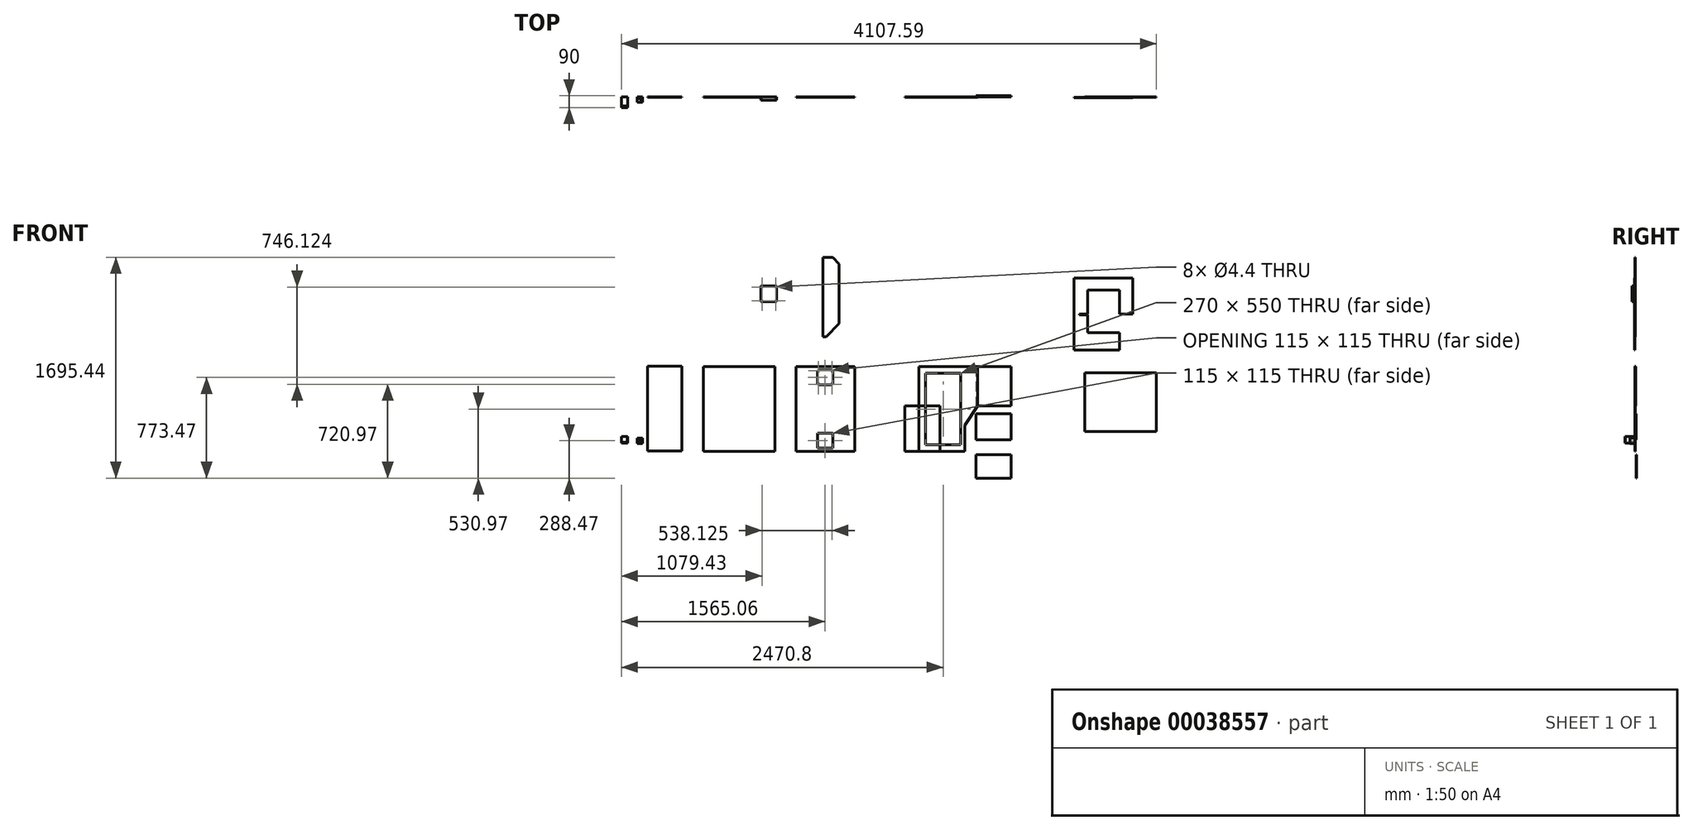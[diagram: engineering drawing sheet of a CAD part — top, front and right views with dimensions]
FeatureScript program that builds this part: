
annotation { "Feature Type Name" : "Feature", "Feature Type Description" : "" }
export const myFeature = defineFeature(function(context is Context, id is Id, definition is map)
    precondition{}
    {
        {
            var Q0;
            Q0=qCreatedBy(makeId("Front.planeOp"),FACE);
            var sketch = newSketch(context, id + "F0", { "sketchPlane" : qUnion([Q0])});
            skLineSegment(sketch, "E0.bottom", {"start": v(-122.86, 100.72) * mm, "end": v(-82.86, 100.72) * mm});
            skLineSegment(sketch, "E0.top", {"start": v(-122.86, 60.72) * mm, "end": v(-82.86, 60.72) * mm});
            skLineSegment(sketch, "E0.left", {"start": v(-122.86, 100.72) * mm, "end": v(-122.86, 60.72) * mm});
            skLineSegment(sketch, "E0.right", {"start": v(-82.86, 100.72) * mm, "end": v(-82.86, 60.72) * mm});
            skSolve(sketch);
        }
        {
            var Q0;
            Q0 = qSketchRegion(id + "F0", true);
            extrude(context, id + "F1", {"entities" : qUnion([Q0]), "depth" : 40 * mm});
        }
        {
            var Q0;
            Q0=makeQuery(id+"F1.opExtrude","SWEPT_FACE",FACE,{"disambiguationData":[OSD([sQuery(id+"F0.wireOp",EDGE,"E0.bottom")])]});
            var sketch = newSketch(context, id + "F2", { "sketchPlane" : qUnion([Q0])});
            skLineSegment(sketch, "E1.bottom", {"start": v(-122.86, -40) * mm, "end": v(-87.86, -40) * mm});
            skLineSegment(sketch, "E1.top", {"start": v(-122.86, -5) * mm, "end": v(-87.86, -5) * mm});
            skLineSegment(sketch, "E1.left", {"start": v(-122.86, -40) * mm, "end": v(-122.86, -5) * mm});
            skLineSegment(sketch, "E1.right", {"start": v(-87.86, -40) * mm, "end": v(-87.86, -5) * mm});
            skSolve(sketch);
        }
        {
            var Q0;
            Q0 = qSketchRegion(id + "F2", true);
            extrude(context, id + "F3", {"entities" : qUnion([Q0]), "operationType" : NewBodyOperationType.REMOVE, "oppositeDirection" : true, "depth" : 20 * mm});
        }
        {
            var Q0;
            Q0=makeQuery(id+"F1.opExtrude","SWEPT_FACE",FACE,{"disambiguationData":[OSD([sQuery(id+"F0.wireOp",EDGE,"E0.top")])]});
            var sketch = newSketch(context, id + "F4", { "sketchPlane" : qUnion([Q0])});
            skLineSegment(sketch, "E2.bottom", {"start": v(-122.86, 40) * mm, "end": v(-87.86, 40) * mm});
            skLineSegment(sketch, "E2.top", {"start": v(-122.86, 5) * mm, "end": v(-87.86, 5) * mm});
            skLineSegment(sketch, "E2.left", {"start": v(-122.86, 40) * mm, "end": v(-122.86, 5) * mm});
            skLineSegment(sketch, "E2.right", {"start": v(-87.86, 40) * mm, "end": v(-87.86, 5) * mm});
            skSolve(sketch);
        }
        {
            var Q0;
            Q0 = qSketchRegion(id + "F4", true);
            extrude(context, id + "F5", {"entities" : qUnion([Q0]), "operationType" : NewBodyOperationType.REMOVE, "oppositeDirection" : true, "depth" : 3 * mm});
        }
        {
            var Q0;
            Q0=makeQuery(id+"F3.boolean.opBoolean","COPY",FACE,{"derivedFrom":makeQuery(id+"F3.opExtrude","CAP_FACE",FACE,{"disambiguationData":[OSD([sQuery(id+"F2.wireOp",EDGE,"E1.bottom"),sQuery(id+"F2.wireOp",EDGE,"E1.top"),sQuery(id+"F2.wireOp",EDGE,"E1.left"),sQuery(id+"F2.wireOp",EDGE,"E1.right")])],"isStart":false})});
            var sketch = newSketch(context, id + "F6", { "sketchPlane" : qUnion([Q0])});
            skLineSegment(sketch, "E3.bottom", {"start": v(-122.86, -40) * mm, "end": v(-96.36, -40) * mm});
            skLineSegment(sketch, "E3.top", {"start": v(-122.86, -13.5) * mm, "end": v(-96.36, -13.5) * mm});
            skLineSegment(sketch, "E3.left", {"start": v(-122.86, -40) * mm, "end": v(-122.86, -13.5) * mm});
            skLineSegment(sketch, "E3.right", {"start": v(-96.36, -40) * mm, "end": v(-96.36, -13.5) * mm});
            skLineSegment(sketch, "E4.bottom", {"start": v(-87.86, -40) * mm, "end": v(-91.36, -40) * mm});
            skLineSegment(sketch, "E4.top", {"start": v(-87.86, -5) * mm, "end": v(-91.36, -5) * mm});
            skLineSegment(sketch, "E4.left", {"start": v(-87.86, -40) * mm, "end": v(-87.86, -5) * mm});
            skLineSegment(sketch, "E4.right", {"start": v(-91.36, -40) * mm, "end": v(-91.36, -8.5) * mm});
            skLineSegment(sketch, "E5.bottom", {"start": v(-122.86, -5) * mm, "end": v(-91.93, -5) * mm});
            skLineSegment(sketch, "E5.top", {"start": v(-122.86, -8.5) * mm, "end": v(-91.36, -8.5) * mm});
            skLineSegment(sketch, "E5.left", {"start": v(-122.86, -5) * mm, "end": v(-122.86, -8.5) * mm});
            skSolve(sketch);
        }
        {
            var Q0;
            Q0=makeQuery(id+"F6.imprint","IMPRINT",FACE,{"disambiguationData":[TD([[makeQuery(id+"F6.imprint","IMPRINT",EDGE,{"derivedFrom":sQuery(id+"F6.wireOp",EDGE,"E3.bottom")}),1.0]])]});
            var Q1;
            Q1=makeQuery(id+"F6.imprint","IMPRINT",FACE,{"disambiguationData":[TD([[makeQuery(id+"F6.imprint","IMPRINT",EDGE,{"derivedFrom":sQuery(id+"F6.wireOp",EDGE,"E4.bottom")}),1.0]])]});
            extrude(context, id + "F7", {"entities" : qUnion([Q0, Q1]), "operationType" : NewBodyOperationType.REMOVE, "oppositeDirection" : true, "depth" : 12 * mm});
        }
        {
            var Q0;
            Q0=qCreatedBy(makeId("Front.planeOp"),FACE);
            var sketch = newSketch(context, id + "F8", { "sketchPlane" : qUnion([Q0])});
            skLineSegment(sketch, "E6.bottom", {"start": v(-44.07, 654.35) * mm, "end": v(220.93, 654.35) * mm});
            skLineSegment(sketch, "E6.top", {"start": v(-44.07, 4.35) * mm, "end": v(220.93, 4.35) * mm});
            skLineSegment(sketch, "E6.left", {"start": v(-44.07, 654.35) * mm, "end": v(-44.07, 4.35) * mm});
            skLineSegment(sketch, "E6.right", {"start": v(220.93, 654.35) * mm, "end": v(220.93, 4.35) * mm});
            skSolve(sketch);
        }
        {
            var Q0;
            Q0=makeQuery(id+"F8.imprint","IMPRINT",FACE,{"disambiguationData":[TD([[makeQuery(id+"F8.imprint","IMPRINT",EDGE,{"derivedFrom":sQuery(id+"F8.wireOp",EDGE,"E6.bottom")}),-1.0]])]});
            extrude(context, id + "F9", {"entities" : qUnion([Q0]), "depth" : 3 * mm});
        }
        {
            var Q0;
            Q0=qCreatedBy(makeId("Front.planeOp"),FACE);
            var sketch = newSketch(context, id + "F10", { "sketchPlane" : qUnion([Q0])});
            skLineSegment(sketch, "E7.bottom", {"start": v(383.87, 0) * mm, "end": v(933.87, 0) * mm});
            skLineSegment(sketch, "E7.top", {"start": v(383.87, 650) * mm, "end": v(933.87, 650) * mm});
            skLineSegment(sketch, "E7.left", {"start": v(383.87, 0) * mm, "end": v(383.87, 650) * mm});
            skLineSegment(sketch, "E7.right", {"start": v(933.87, 0) * mm, "end": v(933.87, 650) * mm});
            skSolve(sketch);
        }
        {
            var Q0;
            Q0=makeQuery(id+"F10.imprint","IMPRINT",FACE,{"disambiguationData":[TD([[makeQuery(id+"F10.imprint","IMPRINT",EDGE,{"derivedFrom":sQuery(id+"F10.wireOp",EDGE,"E7.bottom")}),1.0]])]});
            extrude(context, id + "F11", {"entities" : qUnion([Q0]), "depth" : 3 * mm});
        }
        {
            var Q0;
            Q0=qCreatedBy(makeId("Front.planeOp"),FACE);
            var sketch = newSketch(context, id + "F12", { "sketchPlane" : qUnion([Q0])});
            skLineSegment(sketch, "E8.bottom", {"start": v(1097.15, 0) * mm, "end": v(1547.15, 0) * mm});
            skLineSegment(sketch, "E8.top", {"start": v(1097.15, 650) * mm, "end": v(1547.15, 650) * mm});
            skLineSegment(sketch, "E8.left", {"start": v(1097.15, 0) * mm, "end": v(1097.15, 650) * mm});
            skLineSegment(sketch, "E8.right", {"start": v(1547.15, 0) * mm, "end": v(1547.15, 650) * mm});
            skCircle(sketch, "E9", {"center": v(1267.15, 620) * mm, "radius": 2.2 * mm});
            skCircle(sketch, "E10", {"center": v(1267.15, 515) * mm, "radius": 2.2 * mm});
            skCircle(sketch, "E11", {"center": v(1372.15, 515) * mm, "radius": 2.2 * mm});
            skCircle(sketch, "E12", {"center": v(1372.15, 620) * mm, "radius": 2.2 * mm});
            skLineSegment(sketch, "E13", {"start": v(1262.15, 615) * mm, "end": v(1262.15, 520) * mm});
            skLineSegment(sketch, "E14", {"start": v(1262.15, 520) * mm, "end": v(1272.15, 520) * mm});
            skLineSegment(sketch, "E15", {"start": v(1272.15, 520) * mm, "end": v(1272.15, 510) * mm});
            skLineSegment(sketch, "E16", {"start": v(1272.15, 510) * mm, "end": v(1367.15, 510) * mm});
            skLineSegment(sketch, "E17", {"start": v(1367.15, 510) * mm, "end": v(1367.15, 520) * mm});
            skLineSegment(sketch, "E18", {"start": v(1367.15, 520) * mm, "end": v(1377.15, 520) * mm});
            skLineSegment(sketch, "E19", {"start": v(1377.15, 520) * mm, "end": v(1377.15, 615) * mm});
            skLineSegment(sketch, "E20", {"start": v(1377.15, 615) * mm, "end": v(1367.15, 615) * mm});
            skLineSegment(sketch, "E21", {"start": v(1367.15, 615) * mm, "end": v(1367.15, 625) * mm});
            skLineSegment(sketch, "E22", {"start": v(1367.15, 625) * mm, "end": v(1272.15, 625) * mm});
            skLineSegment(sketch, "E23", {"start": v(1272.15, 625) * mm, "end": v(1272.15, 615) * mm});
            skLineSegment(sketch, "E24", {"start": v(1272.15, 615) * mm, "end": v(1262.15, 615) * mm});
            skPoint(sketch, "E25.firstSnap0", {"position": v(1262.15, 567.5) * mm});
            skPoint(sketch, "E25.oppositeSnap0", {"position": v(1377.15, 567.5) * mm});
            skLineSegment(sketch, "E25.bottom", {"start": v(1262.15, 140) * mm, "end": v(1377.15, 140) * mm});
            skLineSegment(sketch, "E25.top", {"start": v(1262.15, 25) * mm, "end": v(1377.15, 25) * mm});
            skLineSegment(sketch, "E25.left", {"start": v(1262.15, 140) * mm, "end": v(1262.15, 25) * mm});
            skLineSegment(sketch, "E25.right", {"start": v(1377.15, 140) * mm, "end": v(1377.15, 25) * mm});
            skSolve(sketch);
        }
        {
            var Q0;
            Q0=makeQuery(id+"F12.imprint","IMPRINT",FACE,{"disambiguationData":[TD([[makeQuery(id+"F12.imprint","IMPRINT",EDGE,{"derivedFrom":sQuery(id+"F12.wireOp",EDGE,"E8.bottom")}),1.0]])]});
            extrude(context, id + "F13", {"entities" : qUnion([Q0]), "depth" : 3 * mm});
        }
        {
            var Q0;
            Q0=qCreatedBy(makeId("Front.planeOp"),FACE);
            var sketch = newSketch(context, id + "F14", { "sketchPlane" : qUnion([Q0])});
            skLineSegment(sketch, "E26.bottom", {"start": v(1651.35, 0) * mm, "end": v(2201.35, 0) * mm});
            skLineSegment(sketch, "E26.top", {"start": v(1651.35, 650) * mm, "end": v(2201.35, 650) * mm});
            skLineSegment(sketch, "E26.left", {"start": v(1651.35, 0) * mm, "end": v(1651.35, 650) * mm});
            skLineSegment(sketch, "E26.right", {"start": v(2201.35, 0) * mm, "end": v(2201.35, 650) * mm});
            skLineSegment(sketch, "E27.bottom", {"start": v(2201.35, 0) * mm, "end": v(1931.35, 0) * mm});
            skLineSegment(sketch, "E27.top", {"start": v(2201.35, 350) * mm, "end": v(1931.35, 350) * mm});
            skLineSegment(sketch, "E27.left", {"start": v(2201.35, 0) * mm, "end": v(2201.35, 350) * mm});
            skLineSegment(sketch, "E27.right", {"start": v(1931.35, 0) * mm, "end": v(1931.35, 350) * mm});
            skSolve(sketch);
        }
        {
            var Q0;
            Q0=makeQuery(id+"F14.imprint","IMPRINT",FACE,{"disambiguationData":[TD([[makeQuery(id+"F14.imprint","IMPRINT",EDGE,{"derivedFrom":sQuery(id+"F14.wireOp",EDGE,"E26.bottom")}),1.0]])]});
            extrude(context, id + "F15", {"entities" : qUnion([Q0]), "depth" : 3 * mm});
        }
        {
            var Q0;
            Q0=qCreatedBy(makeId("Front.planeOp"),FACE);
            var sketch = newSketch(context, id + "F16", { "sketchPlane" : qUnion([Q0])});
            skLineSegment(sketch, "E28.bottom", {"start": v(2040.4, 0) * mm, "end": v(2390.4, 0) * mm});
            skLineSegment(sketch, "E28.top", {"start": v(2040.4, 650) * mm, "end": v(2390.4, 650) * mm});
            skLineSegment(sketch, "E28.left", {"start": v(2040.4, 0) * mm, "end": v(2040.4, 650) * mm});
            skLineSegment(sketch, "E28.right", {"start": v(2390.4, 0) * mm, "end": v(2390.4, 200) * mm});
            skLineSegment(sketch, "E29", {"start": v(2390.4, 650) * mm, "end": v(2490.4, 650) * mm});
            skLineSegment(sketch, "E30", {"start": v(2490.4, 650) * mm, "end": v(2490.4, 350) * mm});
            skLineSegment(sketch, "E31", {"start": v(2490.4, 350) * mm, "end": v(2390.4, 200) * mm});
            skLineSegment(sketch, "E32.bottom", {"start": v(2360.4, 50) * mm, "end": v(2090.4, 50) * mm});
            skLineSegment(sketch, "E32.top", {"start": v(2360.4, 600) * mm, "end": v(2090.4, 600) * mm});
            skLineSegment(sketch, "E32.left", {"start": v(2360.4, 50) * mm, "end": v(2360.4, 600) * mm});
            skLineSegment(sketch, "E32.right", {"start": v(2090.4, 50) * mm, "end": v(2090.4, 600) * mm});
            skSolve(sketch);
        }
        {
            var Q0;
            Q0=makeQuery(id+"F16.imprint","IMPRINT",FACE,{"disambiguationData":[TD([[makeQuery(id+"F16.imprint","IMPRINT",EDGE,{"derivedFrom":sQuery(id+"F16.wireOp",EDGE,"E28.bottom")}),1.0]])]});
            extrude(context, id + "F17", {"entities" : qUnion([Q0]), "depth" : 3 * mm});
        }
        {
            var Q0;
            Q0=makeQuery(id+"F17.opExtrude","CAP_FACE",FACE,{"disambiguationData":[OSD([sQuery(id+"F16.wireOp",EDGE,"E28.bottom"),sQuery(id+"F16.wireOp",EDGE,"E28.top"),sQuery(id+"F16.wireOp",EDGE,"E28.left"),sQuery(id+"F16.wireOp",EDGE,"E28.right"),sQuery(id+"F16.wireOp",EDGE,"E29"),sQuery(id+"F16.wireOp",EDGE,"E30"),sQuery(id+"F16.wireOp",EDGE,"E31"),sQuery(id+"F16.wireOp",EDGE,"E32.bottom"),sQuery(id+"F16.wireOp",EDGE,"E32.top"),sQuery(id+"F16.wireOp",EDGE,"E32.left"),sQuery(id+"F16.wireOp",EDGE,"E32.right")])],"isStart":true});
            var sketch = newSketch(context, id + "F18", { "sketchPlane" : qUnion([Q0])});
            skLineSegment(sketch, "E33.bottom", {"start": v(-2477.24, 650) * mm, "end": v(-2747.24, 650) * mm});
            skLineSegment(sketch, "E33.top", {"start": v(-2477.24, 350) * mm, "end": v(-2747.24, 350) * mm});
            skLineSegment(sketch, "E33.left", {"start": v(-2477.24, 650) * mm, "end": v(-2477.24, 350) * mm});
            skLineSegment(sketch, "E33.right", {"start": v(-2747.24, 650) * mm, "end": v(-2747.24, 350) * mm});
            skSolve(sketch);
        }
        {
            var Q0;
            Q0=makeQuery(id+"F18.imprint","IMPRINT",FACE,{"disambiguationData":[TD([[makeQuery(id+"F18.imprint","IMPRINT",EDGE,{"derivedFrom":sQuery(id+"F18.wireOp",EDGE,"E33.bottom")}),1.0]])]});
            extrude(context, id + "F19", {"entities" : qUnion([Q0]), "depth" : 3 * mm});
        }
        {
            var Q0;
            Q0=makeQuery(id+"F19.opExtrude","CAP_FACE",FACE,{"disambiguationData":[OSD([sQuery(id+"F18.wireOp",EDGE,"E33.bottom"),sQuery(id+"F18.wireOp",EDGE,"E33.top"),sQuery(id+"F18.wireOp",EDGE,"E33.left"),sQuery(id+"F18.wireOp",EDGE,"E33.right")])],"isStart":false});
            var sketch = newSketch(context, id + "F20", { "sketchPlane" : qUnion([Q0])});
            skLineSegment(sketch, "E34.bottom", {"start": v(-2747.24, 289.38) * mm, "end": v(-2477.24, 289.38) * mm});
            skLineSegment(sketch, "E34.top", {"start": v(-2747.24, 89.38) * mm, "end": v(-2477.24, 89.38) * mm});
            skLineSegment(sketch, "E34.left", {"start": v(-2747.24, 289.38) * mm, "end": v(-2747.24, 89.38) * mm});
            skLineSegment(sketch, "E34.right", {"start": v(-2477.24, 289.38) * mm, "end": v(-2477.24, 89.38) * mm});
            skSolve(sketch);
        }
        {
            var Q0;
            Q0=makeQuery(id+"F20.imprint","IMPRINT",FACE,{"disambiguationData":[TD([[makeQuery(id+"F20.imprint","IMPRINT",EDGE,{"derivedFrom":sQuery(id+"F20.wireOp",EDGE,"E34.bottom")}),-1.0]])]});
            extrude(context, id + "F21", {"entities" : qUnion([Q0]), "depth" : 3 * mm});
        }
        {
            var Q0;
            Q0=makeQuery(id+"F21.opExtrude","CAP_FACE",FACE,{"disambiguationData":[OSD([sQuery(id+"F20.wireOp",EDGE,"E34.bottom"),sQuery(id+"F20.wireOp",EDGE,"E34.top"),sQuery(id+"F20.wireOp",EDGE,"E34.left"),sQuery(id+"F20.wireOp",EDGE,"E34.right")])],"isStart":false});
            var sketch = newSketch(context, id + "F22", { "sketchPlane" : qUnion([Q0])});
            skLineSegment(sketch, "E35.bottom", {"start": v(-2747.24, -25.97) * mm, "end": v(-2477.24, -25.97) * mm});
            skLineSegment(sketch, "E35.top", {"start": v(-2747.24, -205.97) * mm, "end": v(-2477.24, -205.97) * mm});
            skLineSegment(sketch, "E35.left", {"start": v(-2747.24, -25.97) * mm, "end": v(-2747.24, -205.97) * mm});
            skLineSegment(sketch, "E35.right", {"start": v(-2477.24, -25.97) * mm, "end": v(-2477.24, -205.97) * mm});
            skSolve(sketch);
        }
        {
            var Q0;
            Q0=makeQuery(id+"F22.imprint","IMPRINT",FACE,{"disambiguationData":[TD([[makeQuery(id+"F22.imprint","IMPRINT",EDGE,{"derivedFrom":sQuery(id+"F22.wireOp",EDGE,"E35.bottom")}),-1.0]])]});
            extrude(context, id + "F23", {"entities" : qUnion([Q0]), "depth" : 3 * mm});
        }
        {
            var Q0;
            Q0=qCreatedBy(makeId("Front.planeOp"),FACE);
            var sketch = newSketch(context, id + "F24", { "sketchPlane" : qUnion([Q0])});
            skLineSegment(sketch, "E36.bottom", {"start": v(3312.2, 601.65) * mm, "end": v(3862.2, 601.65) * mm});
            skLineSegment(sketch, "E36.top", {"start": v(3312.2, 151.65) * mm, "end": v(3862.2, 151.65) * mm});
            skLineSegment(sketch, "E36.left", {"start": v(3312.2, 601.65) * mm, "end": v(3312.2, 151.65) * mm});
            skLineSegment(sketch, "E36.right", {"start": v(3862.2, 601.65) * mm, "end": v(3862.2, 151.65) * mm});
            skSolve(sketch);
        }
        {
            var Q0;
            Q0 = qSketchRegion(id + "F24", true);
            extrude(context, id + "F25", {"entities" : qUnion([Q0]), "depth" : 3 * mm});
        }
        {
            var Q0;
            Q0=makeQuery(id+"F25.opExtrude","CAP_FACE",FACE,{"disambiguationData":[OSD([sQuery(id+"F24.wireOp",EDGE,"E36.bottom"),sQuery(id+"F24.wireOp",EDGE,"E36.top"),sQuery(id+"F24.wireOp",EDGE,"E36.left"),sQuery(id+"F24.wireOp",EDGE,"E36.right")])],"isStart":false});
            var sketch = newSketch(context, id + "F26", { "sketchPlane" : qUnion([Q0])});
            skLineSegment(sketch, "E37.bottom", {"start": v(3228.82, 1328.95) * mm, "end": v(3678.82, 1328.95) * mm});
            skLineSegment(sketch, "E37.top", {"start": v(3228.82, 778.95) * mm, "end": v(3578.82, 778.95) * mm});
            skLineSegment(sketch, "E37.left", {"start": v(3228.82, 1328.95) * mm, "end": v(3228.82, 778.95) * mm});
            skLineSegment(sketch, "E37.right", {"start": v(3678.82, 1328.95) * mm, "end": v(3678.82, 1053.95) * mm});
            skLineSegment(sketch, "E38", {"start": v(3578.82, 1053.95) * mm, "end": v(3578.82, 1237.95) * mm});
            skLineSegment(sketch, "E39", {"start": v(3578.82, 1237.95) * mm, "end": v(3335.82, 1237.95) * mm});
            skLineSegment(sketch, "E40", {"start": v(3335.82, 1237.95) * mm, "end": v(3335.82, 1053.95) * mm});
            skLineSegment(sketch, "E41", {"start": v(3335.82, 1053.95) * mm, "end": v(3269.82, 1053.95) * mm});
            skLineSegment(sketch, "E42", {"start": v(3269.82, 1053.95) * mm, "end": v(3269.82, 1047.45) * mm});
            skLineSegment(sketch, "E43", {"start": v(3269.82, 1047.45) * mm, "end": v(3335.82, 1047.45) * mm});
            skLineSegment(sketch, "E44", {"start": v(3335.82, 1047.45) * mm, "end": v(3335.82, 911.95) * mm});
            skLineSegment(sketch, "E45", {"start": v(3578.82, 1053.95) * mm, "end": v(3678.82, 1053.95) * mm});
            skLineSegment(sketch, "E46", {"start": v(3335.82, 911.95) * mm, "end": v(3578.82, 911.95) * mm});
            skLineSegment(sketch, "E47", {"start": v(3578.82, 911.95) * mm, "end": v(3578.82, 778.95) * mm});
            skPoint(sketch, "E48.orphan", {"position": v(3678.82, 778.95) * mm});
            skSolve(sketch);
        }
        {
            var Q0;
            Q0=makeQuery(id+"F26.imprint","IMPRINT",FACE,{"disambiguationData":[TD([[makeQuery(id+"F26.imprint","IMPRINT",EDGE,{"derivedFrom":sQuery(id+"F26.wireOp",EDGE,"E37.bottom")}),-1.0]])]});
            extrude(context, id + "F27", {"entities" : qUnion([Q0]), "depth" : 3 * mm});
        }
        {
            var Q0;
            Q0=qCreatedBy(makeId("Front.planeOp"),FACE);
            var sketch = newSketch(context, id + "F28", { "sketchPlane" : qUnion([Q0])});
            skLineSegment(sketch, "E49.bottom", {"start": v(-245.4, 114.34) * mm, "end": v(-195.4, 114.34) * mm});
            skLineSegment(sketch, "E49.top", {"start": v(-245.4, 64.34) * mm, "end": v(-195.4, 64.34) * mm});
            skLineSegment(sketch, "E49.left", {"start": v(-245.4, 114.34) * mm, "end": v(-245.4, 64.34) * mm});
            skLineSegment(sketch, "E49.right", {"start": v(-195.4, 114.34) * mm, "end": v(-195.4, 64.34) * mm});
            skSolve(sketch);
        }
        {
            var Q0;
            Q0=makeQuery(id+"F28.imprint","IMPRINT",FACE,{"disambiguationData":[TD([[makeQuery(id+"F28.imprint","IMPRINT",EDGE,{"derivedFrom":sQuery(id+"F28.wireOp",EDGE,"E49.bottom")}),-1.0]])]});
            extrude(context, id + "F29", {"entities" : qUnion([Q0]), "depth" : 81 * mm});
        }
        {
            var Q0;
            Q0=makeQuery(id+"F29.opExtrude","CAP_FACE",FACE,{"disambiguationData":[OSD([sQuery(id+"F28.wireOp",EDGE,"E49.bottom"),sQuery(id+"F28.wireOp",EDGE,"E49.top"),sQuery(id+"F28.wireOp",EDGE,"E49.left"),sQuery(id+"F28.wireOp",EDGE,"E49.right")])],"isStart":false});
            var sketch = newSketch(context, id + "F30", { "sketchPlane" : qUnion([Q0])});
            skLineSegment(sketch, "E50.bottom", {"start": v(-245.4, 114.34) * mm, "end": v(-200.4, 114.34) * mm});
            skLineSegment(sketch, "E50.top", {"start": v(-245.4, 69.34) * mm, "end": v(-200.4, 69.34) * mm});
            skLineSegment(sketch, "E50.left", {"start": v(-245.4, 114.34) * mm, "end": v(-245.4, 69.34) * mm});
            skLineSegment(sketch, "E50.right", {"start": v(-200.4, 114.34) * mm, "end": v(-200.4, 69.34) * mm});
            skSolve(sketch);
        }
        {
            var Q0;
            Q0=makeQuery(id+"F30.imprint","IMPRINT",FACE,{"disambiguationData":[TD([[makeQuery(id+"F30.imprint","IMPRINT",EDGE,{"derivedFrom":sQuery(id+"F30.wireOp",EDGE,"E50.bottom")}),-1.0]])]});
            extrude(context, id + "F31", {"entities" : qUnion([Q0]), "operationType" : NewBodyOperationType.REMOVE, "oppositeDirection" : true, "depth" : 10 * mm});
        }
        {
            var Q0;
            Q0=qCreatedBy(makeId("Front.planeOp"),FACE);
            var sketch = newSketch(context, id + "F32", { "sketchPlane" : qUnion([Q0])});
            skLineSegment(sketch, "E51.bottom", {"start": v(826.53, 1268.62) * mm, "end": v(946.53, 1268.62) * mm});
            skLineSegment(sketch, "E51.top", {"start": v(826.53, 1148.62) * mm, "end": v(946.53, 1148.62) * mm});
            skLineSegment(sketch, "E51.left", {"start": v(826.53, 1268.62) * mm, "end": v(826.53, 1148.62) * mm});
            skLineSegment(sketch, "E51.right", {"start": v(946.53, 1268.62) * mm, "end": v(946.53, 1148.62) * mm});
            skCircle(sketch, "E52", {"center": v(834.03, 1261.12) * mm, "radius": 2.2 * mm});
            skCircle(sketch, "E53", {"center": v(834.03, 1156.12) * mm, "radius": 2.2 * mm});
            skCircle(sketch, "E54", {"center": v(939.03, 1156.12) * mm, "radius": 2.2 * mm});
            skCircle(sketch, "E55", {"center": v(939.03, 1261.12) * mm, "radius": 2.2 * mm});
            skSolve(sketch);
        }
        {
            var Q0;
            Q0=makeQuery(id+"F32.imprint","IMPRINT",FACE,{"disambiguationData":[TD([[makeQuery(id+"F32.imprint","IMPRINT",EDGE,{"derivedFrom":sQuery(id+"F32.wireOp",EDGE,"E51.bottom")}),-1.0]])]});
            extrude(context, id + "F33", {"entities" : qUnion([Q0]), "depth" : 25 * mm});
        }
        {
            var Q0;
            Q0=qCreatedBy(makeId("Front.planeOp"),FACE);
            var sketch = newSketch(context, id + "F34", { "sketchPlane" : qUnion([Q0])});
            skLineSegment(sketch, "E56", {"start": v(1301.87, 879.47) * mm, "end": v(1301.87, 1489.47) * mm});
            skLineSegment(sketch, "E57", {"start": v(1301.87, 1489.47) * mm, "end": v(1376.87, 1489.47) * mm});
            skLineSegment(sketch, "E58", {"start": v(1376.87, 1489.47) * mm, "end": v(1426.87, 1439.47) * mm});
            skLineSegment(sketch, "E59", {"start": v(1426.87, 1439.47) * mm, "end": v(1426.87, 979.47) * mm});
            skLineSegment(sketch, "E60", {"start": v(1426.87, 979.47) * mm, "end": v(1326.87, 879.47) * mm});
            skLineSegment(sketch, "E61", {"start": v(1326.87, 879.47) * mm, "end": v(1301.87, 879.47) * mm});
            skPoint(sketch, "E62.orphan", {"position": v(1301.87, 960.84) * mm});
            skSolve(sketch);
        }
        {
            var Q0;
            Q0=makeQuery(id+"F34.imprint","IMPRINT",FACE,{"disambiguationData":[TD([[makeQuery(id+"F34.imprint","IMPRINT",EDGE,{"derivedFrom":sQuery(id+"F34.wireOp",EDGE,"E56")}),-1.0]])]});
            extrude(context, id + "F35", {"entities" : qUnion([Q0]), "depth" : 3 * mm});
        }
    });
